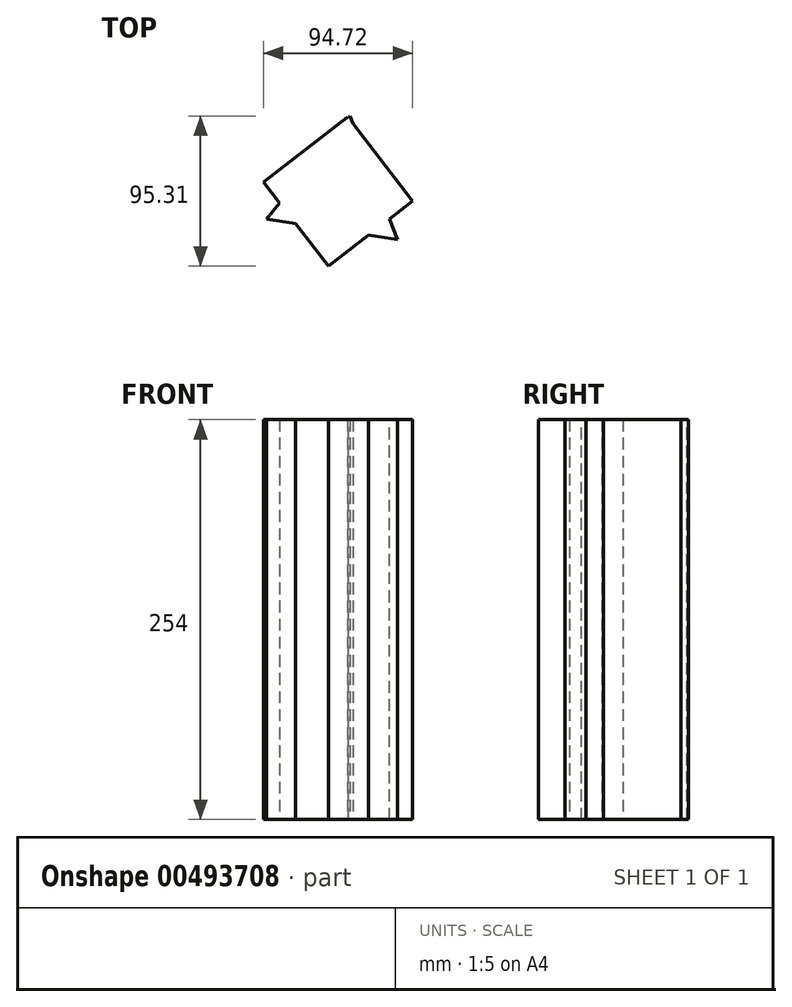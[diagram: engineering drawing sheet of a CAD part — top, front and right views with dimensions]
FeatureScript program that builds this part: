
annotation { "Feature Type Name" : "Feature", "Feature Type Description" : "" }
export const myFeature = defineFeature(function(context is Context, id is Id, definition is map)
    precondition{}
    {
        {
            var Q0;
            Q0=qCreatedBy(makeId("Top.planeOp"),FACE);
            var sketch = newSketch(context, id + "F0", { "sketchPlane" : qUnion([Q0])});
            skCircle(sketch, "E0.cCircle", {"center": v(0, 0) * mm, "radius": 47.76 * mm, "construction": true});
            skLineSegment(sketch, "E0.0", {"start": v(-6.12, -47.36) * mm, "end": v(-47.36, 6.12) * mm});
            skLineSegment(sketch, "E0.1", {"start": v(-47.36, 6.12) * mm, "end": v(6.12, 47.36) * mm});
            skLineSegment(sketch, "E0.2", {"start": v(6.12, 47.36) * mm, "end": v(47.36, -6.12) * mm});
            skLineSegment(sketch, "E0.3", {"start": v(47.36, -6.12) * mm, "end": v(-6.12, -47.36) * mm});
            skSolve(sketch);
        }
        {
            var Q0;
            Q0=qCreatedBy(makeId("Top.planeOp"),FACE);
            var sketch = newSketch(context, id + "F1", { "sketchPlane" : qUnion([Q0])});
            skCircle(sketch, "E1.cCircle", {"center": v(0, 0) * mm, "radius": 48.54 * mm, "construction": true});
            skLineSegment(sketch, "E1.0", {"start": v(7.58, 47.95) * mm, "end": v(37.73, -30.54) * mm});
            skLineSegment(sketch, "E1.1", {"start": v(37.73, -30.54) * mm, "end": v(-45.31, -17.41) * mm});
            skLineSegment(sketch, "E1.2", {"start": v(-45.31, -17.41) * mm, "end": v(7.58, 47.95) * mm});
            skSolve(sketch);
        }
        {
            var Q0;
            Q0=makeQuery(id+"F0.imprint","IMPRINT",FACE,{"disambiguationData":[TD([[makeQuery(id+"F0.imprint","IMPRINT",EDGE,{"derivedFrom":sQuery(id+"F0.wireOp",EDGE,"E0.0")}),-1.0]])]});
            extrude(context, id + "F2", {"entities" : qUnion([Q0]), "depth" : 254 * mm});
        }
        {
            var Q0;
            Q0=makeQuery(id+"F1.imprint","IMPRINT",FACE,{"disambiguationData":[TD([[makeQuery(id+"F1.imprint","IMPRINT",EDGE,{"derivedFrom":sQuery(id+"F1.wireOp",EDGE,"E1.0")}),-1.0]])]});
            extrude(context, id + "F3", {"entities" : qUnion([Q0]), "operationType" : NewBodyOperationType.ADD, "depth" : 254 * mm});
        }
    });
